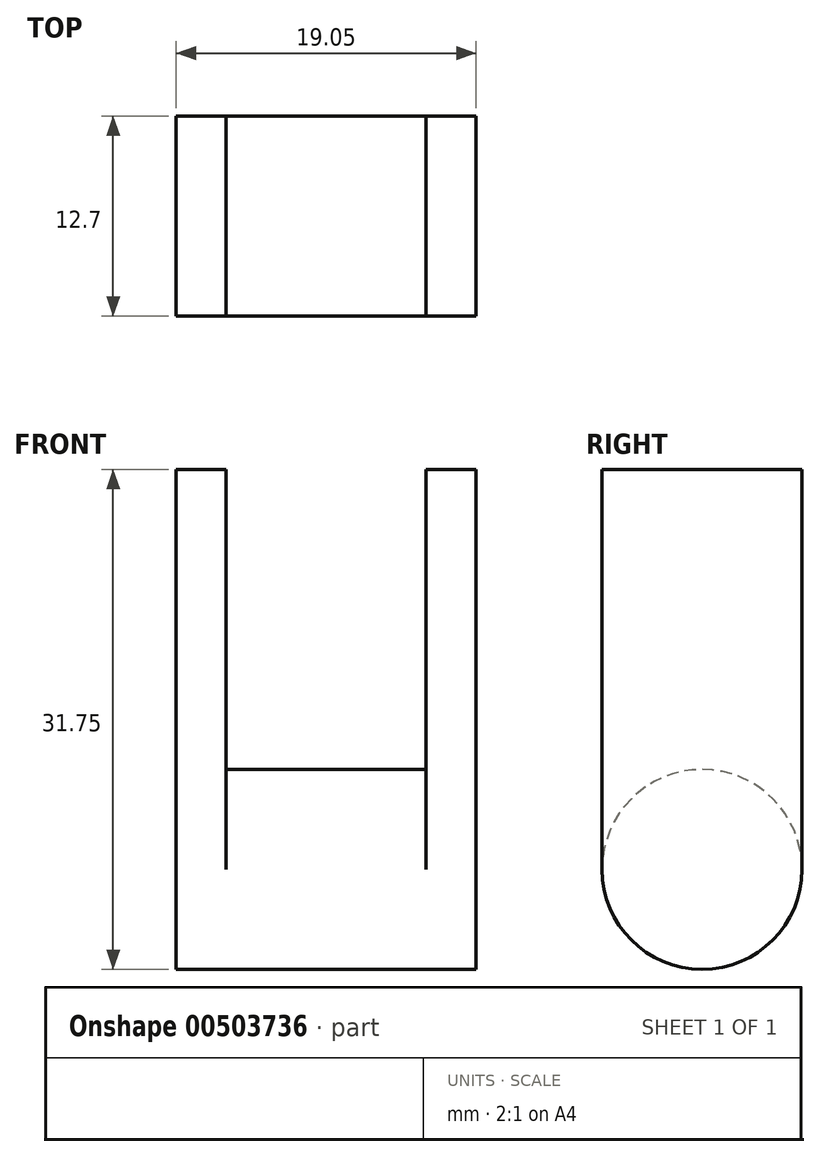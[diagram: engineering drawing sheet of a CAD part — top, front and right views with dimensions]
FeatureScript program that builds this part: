
annotation { "Feature Type Name" : "Feature", "Feature Type Description" : "" }
export const myFeature = defineFeature(function(context is Context, id is Id, definition is map)
    precondition{}
    {
        {
            var Q0;
            Q0=qCreatedBy(makeId("Right.planeOp"),FACE);
            var sketch = newSketch(context, id + "F0", { "sketchPlane" : qUnion([Q0])});
            skCircle(sketch, "E0", {"center": v(0, 0) * mm, "radius": 6.35 * mm});
            skPoint(sketch, "E1", {"position": v(-6.35, 0) * mm});
            skPoint(sketch, "E2", {"position": v(6.35, 0) * mm});
            skLineSegment(sketch, "E3", {"start": v(-6.35, 0) * mm, "end": v(-6.35, 25.4) * mm});
            skLineSegment(sketch, "E4", {"start": v(6.35, 0) * mm, "end": v(6.35, 25.4) * mm});
            skLineSegment(sketch, "E5", {"start": v(6.35, 25.4) * mm, "end": v(-6.35, 25.4) * mm});
            skSolve(sketch);
        }
        {
            var Q0;
            {var subQ0=sQuery(id+"F0.wireOp",EDGE,"E0");var subQ1=makeQuery(id+"F0.imprint","INTERSECT",VERTEX,{"derivedFrom":[subQ0,sQuery(id+"F0.wireOp",EDGE,"E3")]});Q0=makeQuery(id+"F0.imprint","IMPRINT",FACE,{"disambiguationData":[TD([[makeQuery(id+"F0.imprint","IMPRINT",EDGE,{"disambiguationData":[TD([[subQ1,1.0]])],"derivedFrom":subQ0}),1.0]])]});}
            extrude(context, id + "F1", {"entities" : qUnion([Q0]), "depth" : 19.05 * mm, "offsetDistance" : 25.4 * mm});
        }
        {
            var Q0;
            Q0 = qSketchRegion(id + "F0", true);
            extrude(context, id + "F2", {"entities" : qUnion([Q0]), "operationType" : NewBodyOperationType.ADD, "depth" : 3.17 * mm, "offsetDistance" : 25.4 * mm});
        }
        {
            var Q0;
            Q0=makeQuery(id+"F1.opExtrude","CAP_FACE",FACE,{"disambiguationData":[OSD([sQuery(id+"F0.wireOp",EDGE,"E0")])],"isStart":false});
            var sketch = newSketch(context, id + "F3", { "sketchPlane" : qUnion([Q0])});
            skLineSegment(sketch, "E6", {"start": v(-6.35, 0) * mm, "end": v(-6.35, 25.4) * mm});
            skLineSegment(sketch, "E7", {"start": v(-6.35, 25.4) * mm, "end": v(6.35, 25.4) * mm});
            skLineSegment(sketch, "E8", {"start": v(6.35, 25.4) * mm, "end": v(6.35, 0) * mm});
            skLineSegment(sketch, "E9", {"start": v(-6.35, 0) * mm, "end": v(6.35, 0) * mm});
            skSolve(sketch);
        }
        {
            var Q0;
            {var subQ0=sQuery(id+"F3.wireOp",EDGE,"E6");Q0=makeQuery(id+"F3.imprint","IMPRINT",FACE,{"disambiguationData":[TD([[makeQuery(id+"F3.imprint","IMPRINT",EDGE,{"derivedFrom":subQ0}),-1.0]])]});}
            extrude(context, id + "F4", {"entities" : qUnion([Q0]), "operationType" : NewBodyOperationType.ADD, "depth" : -3.17 * mm, "offsetDistance" : 25.4 * mm});
        }
    });
